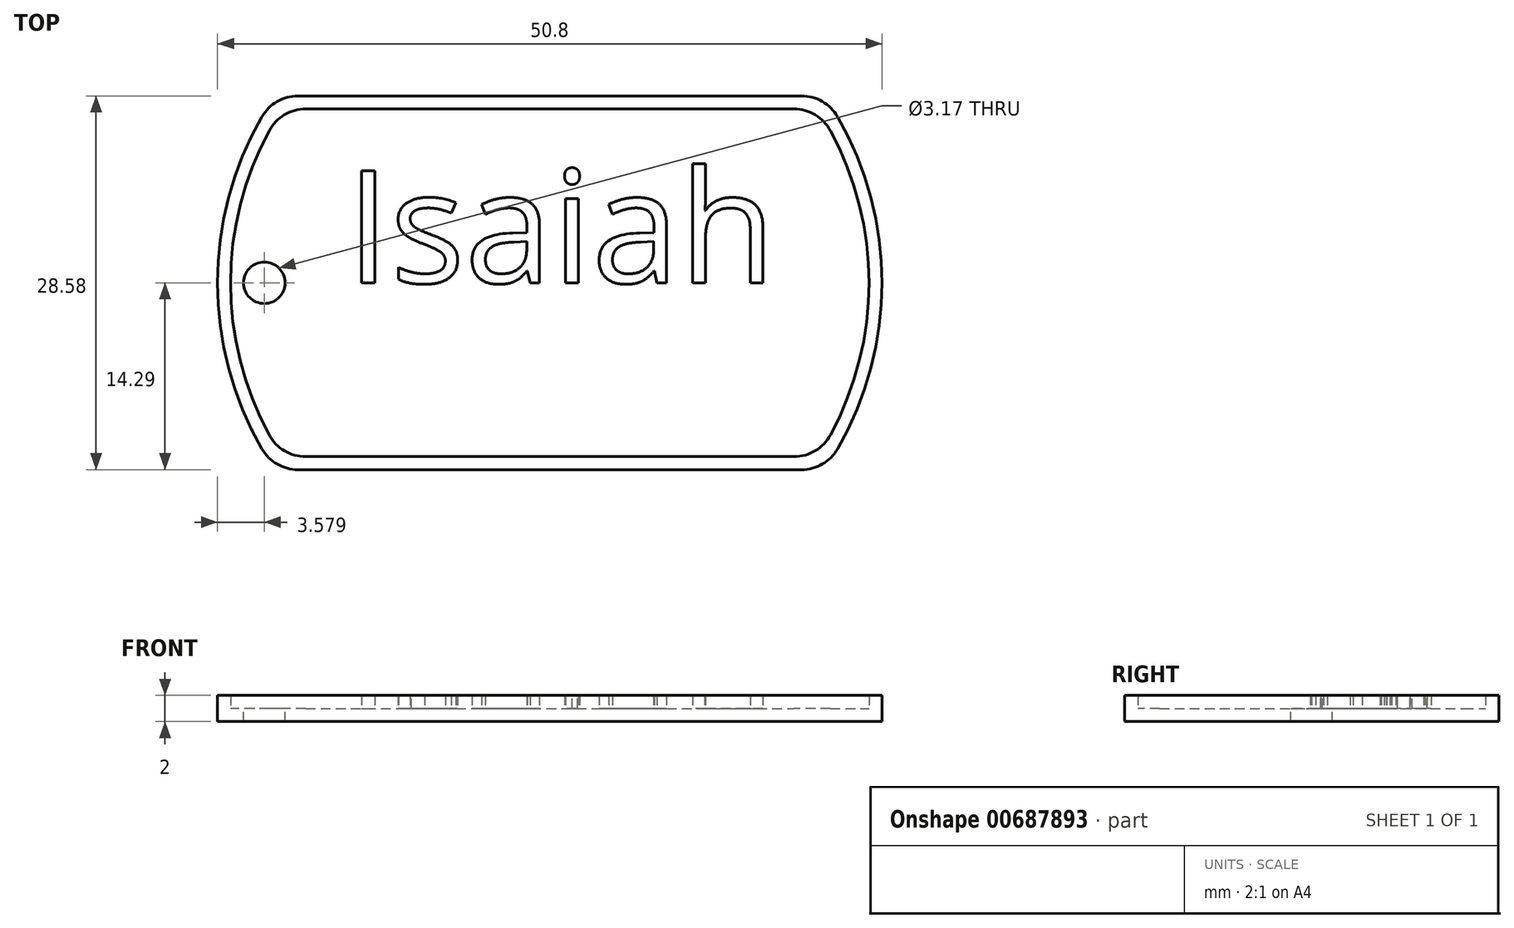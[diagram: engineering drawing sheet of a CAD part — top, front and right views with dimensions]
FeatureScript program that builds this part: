
annotation { "Feature Type Name" : "Feature", "Feature Type Description" : "" }
export const myFeature = defineFeature(function(context is Context, id is Id, definition is map)
    precondition{}
    {
        {
            var Q0;
            Q0=qCreatedBy(makeId("Top.planeOp"),FACE);
            var sketch = newSketch(context, id + "F0", { "sketchPlane" : qUnion([Q0])});
            skArc(sketch, "E0", {"start": v(-22, 12.7) * mm, "mid": v(-25.4, 0) * mm, "end": v(-22, -12.7) * mm});
            skLineSegment(sketch, "E1.top", {"start": v(-19.25, -14.29) * mm, "end": v(19.25, -14.29) * mm});
            skArc(sketch, "E2.trimOffspring", {"start": v(22, -12.7) * mm, "mid": v(25.4, 0) * mm, "end": v(22, 12.7) * mm});
            skLineSegment(sketch, "E3", {"start": v(-19.25, 14.29) * mm, "end": v(19.25, 14.29) * mm});
            skPoint(sketch, "E4.visualSharp", {"position": v(-21, 14.29) * mm});
            skArc(sketch, "E4.filletArc", {"start": v(-19.25, 14.29) * mm, "mid": v(-20.83, 13.86) * mm, "end": v(-22, 12.7) * mm});
            skPoint(sketch, "E5.visualSharp", {"position": v(21, 14.29) * mm});
            skArc(sketch, "E5.filletArc", {"start": v(22, 12.7) * mm, "mid": v(20.83, 13.86) * mm, "end": v(19.25, 14.29) * mm});
            skPoint(sketch, "E6.visualSharp", {"position": v(21, -14.29) * mm});
            skArc(sketch, "E6.filletArc", {"start": v(19.25, -14.29) * mm, "mid": v(20.83, -13.86) * mm, "end": v(22, -12.7) * mm});
            skPoint(sketch, "E7.visualSharp", {"position": v(-21, -14.29) * mm});
            skArc(sketch, "E7.filletArc", {"start": v(-22, -12.7) * mm, "mid": v(-20.83, -13.86) * mm, "end": v(-19.25, -14.29) * mm});
            skSolve(sketch);
        }
        {
            var Q0;
            Q0=makeQuery(id+"F0.imprint","IMPRINT",FACE,{"disambiguationData":[TD([[makeQuery(id+"F0.imprint","IMPRINT",EDGE,{"derivedFrom":sQuery(id+"F0.wireOp",EDGE,"E0")}),1.0]])]});
            extrude(context, id + "F1", {"entities" : qUnion([Q0]), "depth" : 1 * mm, "offsetDistance" : 25.4 * mm});
        }
        {
            var Q0;
            Q0=makeQuery(id+"F1.opExtrude","CAP_FACE",FACE,{"disambiguationData":[OSD([sQuery(id+"F0.wireOp",EDGE,"E0"),sQuery(id+"F0.wireOp",EDGE,"E1.top"),sQuery(id+"F0.wireOp",EDGE,"E2.trimOffspring"),sQuery(id+"F0.wireOp",EDGE,"E3"),sQuery(id+"F0.wireOp",EDGE,"E4.filletArc"),sQuery(id+"F0.wireOp",EDGE,"E5.filletArc"),sQuery(id+"F0.wireOp",EDGE,"E6.filletArc"),sQuery(id+"F0.wireOp",EDGE,"E7.filletArc")])],"isStart":false});
            var sketch = newSketch(context, id + "F2", { "sketchPlane" : qUnion([Q0])});
            skLineSegment(sketch, "E8.0", {"start": v(-18.66, 13.29) * mm, "end": v(18.66, 13.29) * mm});
            skArc(sketch, "E8.1", {"start": v(-21.45, 11.63) * mm, "mid": v(-24.4, 0) * mm, "end": v(-21.45, -11.63) * mm});
            skLineSegment(sketch, "E8.2", {"start": v(-18.66, -13.29) * mm, "end": v(18.66, -13.29) * mm});
            skArc(sketch, "E8.3", {"start": v(21.45, -11.63) * mm, "mid": v(24.4, 0) * mm, "end": v(21.45, 11.63) * mm});
            skPoint(sketch, "E9.visualSharp", {"position": v(-20.46, 13.29) * mm});
            skArc(sketch, "E9.filletArc", {"start": v(-18.66, 13.29) * mm, "mid": v(-20.29, 12.84) * mm, "end": v(-21.45, 11.63) * mm});
            skPoint(sketch, "E10.visualSharp", {"position": v(20.46, 13.29) * mm});
            skArc(sketch, "E10.filletArc", {"start": v(21.45, 11.63) * mm, "mid": v(20.29, 12.84) * mm, "end": v(18.66, 13.29) * mm});
            skPoint(sketch, "E11.visualSharp", {"position": v(20.46, -13.29) * mm});
            skArc(sketch, "E11.filletArc", {"start": v(18.66, -13.29) * mm, "mid": v(20.29, -12.84) * mm, "end": v(21.45, -11.63) * mm});
            skPoint(sketch, "E12.visualSharp", {"position": v(-20.46, -13.29) * mm});
            skArc(sketch, "E12.filletArc", {"start": v(-21.45, -11.63) * mm, "mid": v(-20.29, -12.84) * mm, "end": v(-18.66, -13.29) * mm});
            skLineSegment(sketch, "E13.0", {"start": v(-19.25, 14.29) * mm, "end": v(19.25, 14.29) * mm});
            skArc(sketch, "E13.1", {"start": v(-22, 12.7) * mm, "mid": v(-25.4, 0) * mm, "end": v(-22, -12.7) * mm});
            skLineSegment(sketch, "E13.2", {"start": v(-19.25, -14.29) * mm, "end": v(19.25, -14.29) * mm});
            skArc(sketch, "E13.3", {"start": v(22, -12.7) * mm, "mid": v(25.4, 0) * mm, "end": v(22, 12.7) * mm});
            skPoint(sketch, "E14.visualSharp", {"position": v(-21, -14.29) * mm});
            skArc(sketch, "E14.filletArc", {"start": v(-22, -12.7) * mm, "mid": v(-20.83, -13.86) * mm, "end": v(-19.25, -14.29) * mm});
            skPoint(sketch, "E15.visualSharp", {"position": v(21, -14.29) * mm});
            skArc(sketch, "E15.filletArc", {"start": v(19.25, -14.29) * mm, "mid": v(20.83, -13.86) * mm, "end": v(22, -12.7) * mm});
            skPoint(sketch, "E16.visualSharp", {"position": v(21, 14.29) * mm});
            skArc(sketch, "E16.filletArc", {"start": v(22, 12.7) * mm, "mid": v(20.83, 13.86) * mm, "end": v(19.25, 14.29) * mm});
            skPoint(sketch, "E17.visualSharp", {"position": v(-21, 14.29) * mm});
            skArc(sketch, "E17.filletArc", {"start": v(-19.25, 14.29) * mm, "mid": v(-20.83, 13.86) * mm, "end": v(-22, 12.7) * mm});
            skSolve(sketch);
        }
        {
            var Q0;
            Q0=makeQuery(id+"F2.imprint","IMPRINT",FACE,{"disambiguationData":[TD([[makeQuery(id+"F2.imprint","IMPRINT",EDGE,{"derivedFrom":sQuery(id+"F2.wireOp",EDGE,"E8.0")}),1.0]])]});
            extrude(context, id + "F3", {"entities" : qUnion([Q0]), "operationType" : NewBodyOperationType.ADD, "depth" : 1 * mm, "offsetDistance" : 25.4 * mm});
        }
        {
            var Q0;
            Q0=makeQuery(id+"F1.opExtrude","CAP_FACE",FACE,{"disambiguationData":[OSD([sQuery(id+"F0.wireOp",EDGE,"E0"),sQuery(id+"F0.wireOp",EDGE,"E1.top"),sQuery(id+"F0.wireOp",EDGE,"E2.trimOffspring"),sQuery(id+"F0.wireOp",EDGE,"E3"),sQuery(id+"F0.wireOp",EDGE,"E4.filletArc"),sQuery(id+"F0.wireOp",EDGE,"E5.filletArc"),sQuery(id+"F0.wireOp",EDGE,"E6.filletArc"),sQuery(id+"F0.wireOp",EDGE,"E7.filletArc")])],"isStart":false});
            var sketch = newSketch(context, id + "F4", { "sketchPlane" : qUnion([Q0])});
            skCircle(sketch, "E18", {"center": v(-21.82, 0) * mm, "radius": 1.59 * mm});
            skSolve(sketch);
        }
        {
            var Q0;
            Q0=makeQuery(id+"F4.imprint","IMPRINT",FACE,{"disambiguationData":[TD([[makeQuery(id+"F4.imprint","IMPRINT",EDGE,{"derivedFrom":sQuery(id+"F4.wireOp",EDGE,"E18")}),1.0]])]});
            extrude(context, id + "F5", {"entities" : qUnion([Q0]), "operationType" : NewBodyOperationType.REMOVE, "oppositeDirection" : true, "depth" : 1 * mm, "offsetDistance" : 25.4 * mm});
        }
        {
            var Q0;
            Q0=makeQuery(id+"F2.imprint","IMPRINT",FACE,{"disambiguationData":[TD([[makeQuery(id+"F2.imprint","IMPRINT",EDGE,{"derivedFrom":sQuery(id+"F2.wireOp",EDGE,"E8.0")}),-1.0]])]});
            var sketch = newSketch(context, id + "F6", { "sketchPlane" : qUnion([Q0])});
            skText(sketch, "E19", { "text": "Isaiah", "fontName": "OpenSans-Regular.ttf"});
            const initialGuessF6  = {"E19": [-0.01556, 0, 1, 0, 0.00864]};
            skSetInitialGuess(sketch, initialGuessF6);
            skSolve(sketch);
        }
        {
            var Q0;
            Q0 = qSketchRegion(id + "F6", true);
            extrude(context, id + "F7", {"entities" : qUnion([Q0]), "operationType" : NewBodyOperationType.ADD, "depth" : 1 * mm, "offsetDistance" : 25.4 * mm});
        }
    });
